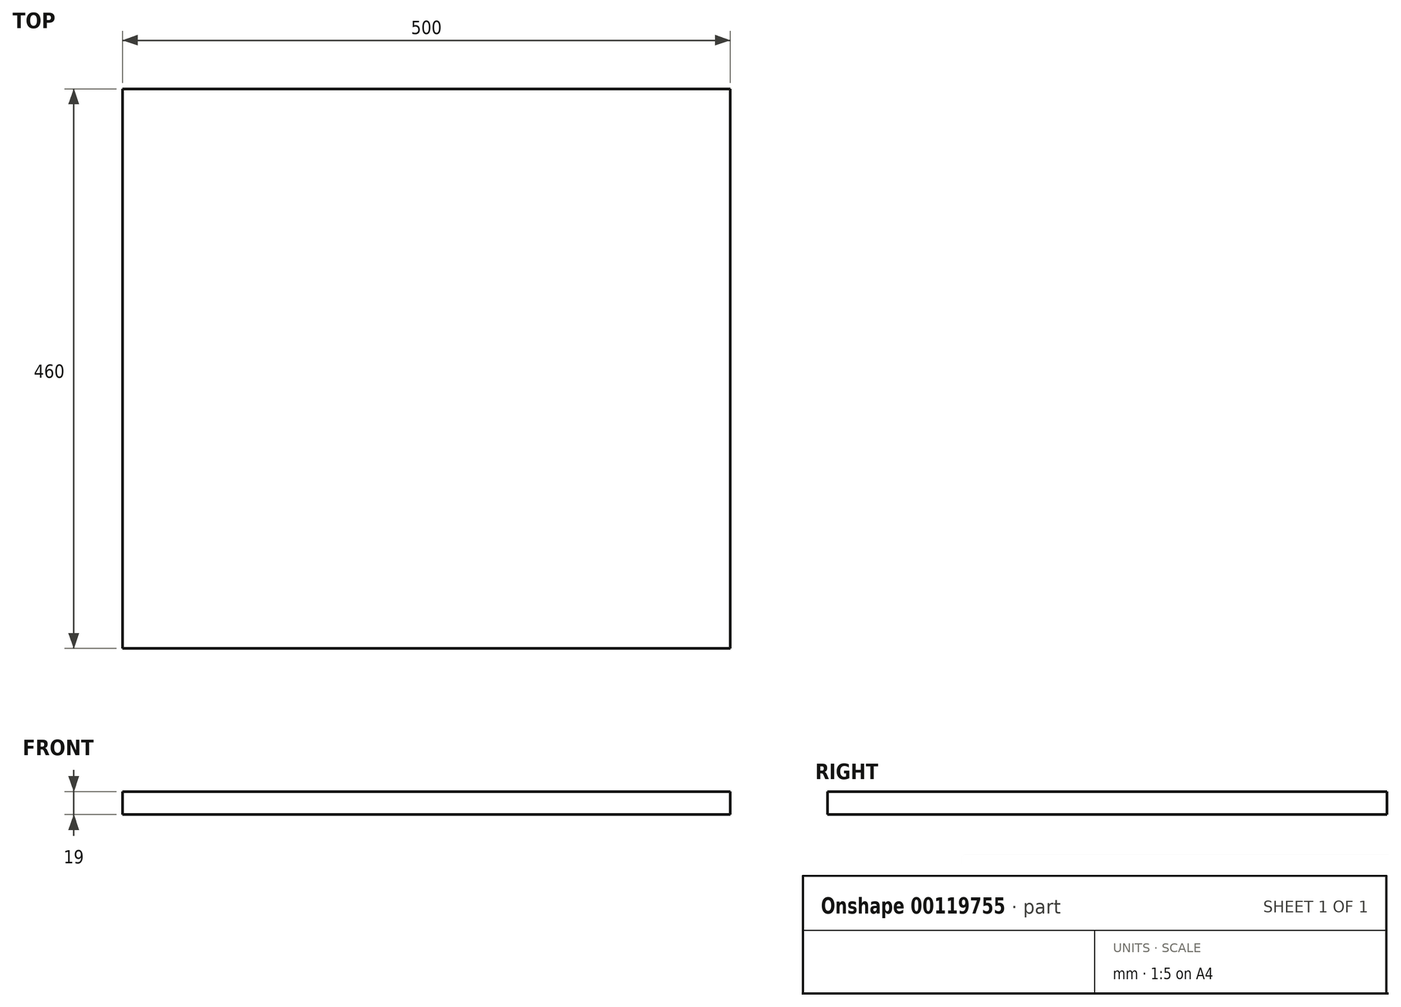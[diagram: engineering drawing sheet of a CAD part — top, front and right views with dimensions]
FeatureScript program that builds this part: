
annotation { "Feature Type Name" : "Feature", "Feature Type Description" : "" }
export const myFeature = defineFeature(function(context is Context, id is Id, definition is map)
    precondition{}
    {
        {
            var Q0;
            Q0=qCreatedBy(makeId("Top.planeOp"),FACE);
            var sketch = newSketch(context, id + "F0", { "sketchPlane" : qUnion([Q0])});
            skLineSegment(sketch, "E0.bottom", {"start": v(-250, 230) * mm, "end": v(250, 230) * mm});
            skLineSegment(sketch, "E0.top", {"start": v(-250, -230) * mm, "end": v(250, -230) * mm});
            skLineSegment(sketch, "E0.left", {"start": v(-250, 230) * mm, "end": v(-250, -230) * mm});
            skLineSegment(sketch, "E0.right", {"start": v(250, 230) * mm, "end": v(250, -230) * mm});
            skPoint(sketch, "E0.middle", {"position": v(0, 0) * mm});
            skSolve(sketch);
        }
        {
            var Q0;
            Q0 = qSketchRegion(id + "F0", true);
            extrude(context, id + "F1", {"entities" : qUnion([Q0]), "depth" : 19 * mm});
        }
    });
